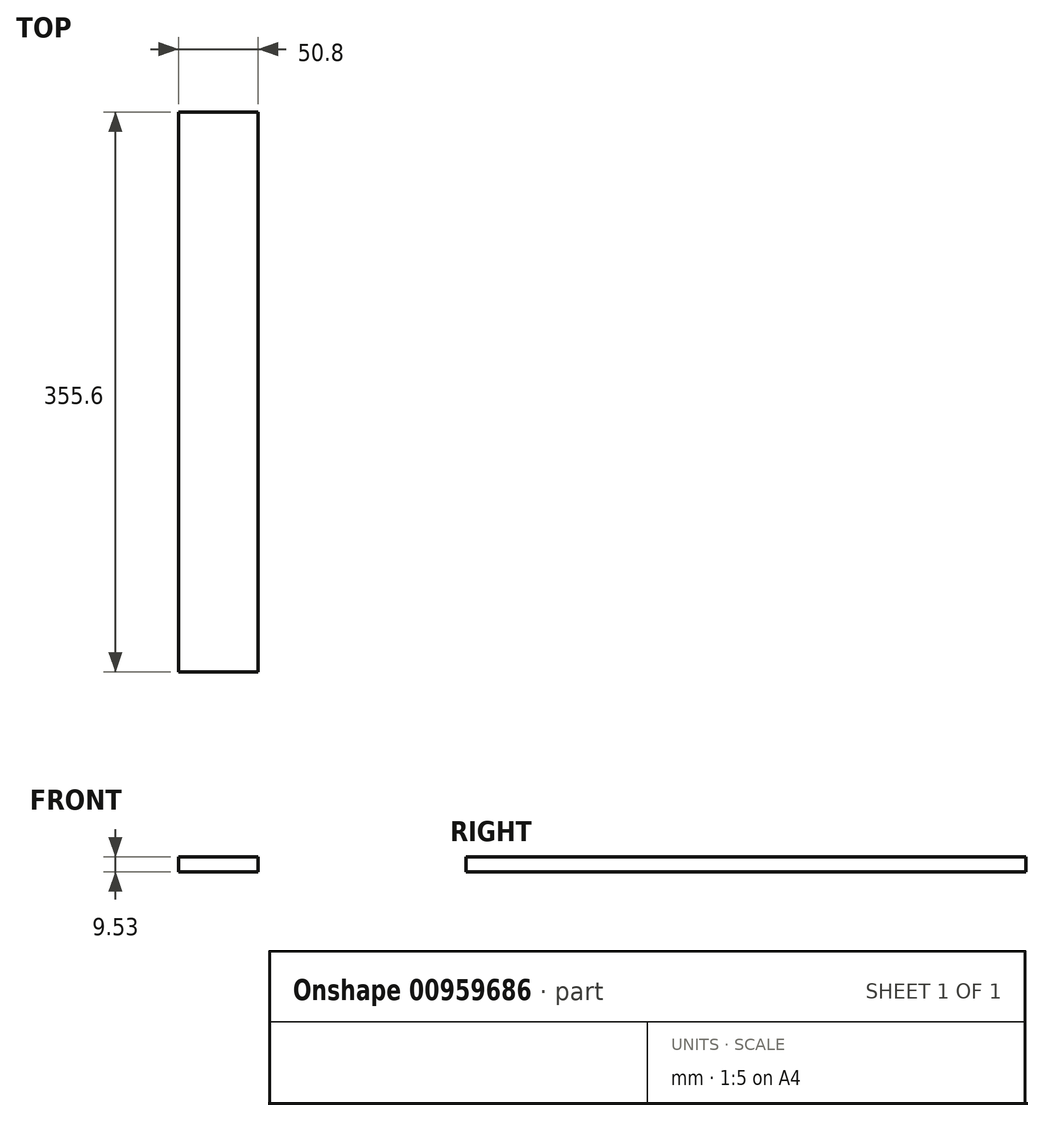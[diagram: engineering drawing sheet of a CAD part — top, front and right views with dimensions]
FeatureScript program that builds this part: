
annotation { "Feature Type Name" : "Feature", "Feature Type Description" : "" }
export const myFeature = defineFeature(function(context is Context, id is Id, definition is map)
    precondition{}
    {
        {
            var Q0;
            Q0=qCreatedBy(makeId("Top.planeOp"),FACE);
            var sketch = newSketch(context, id + "F0", { "sketchPlane" : qUnion([Q0])});
            skLineSegment(sketch, "E0.bottom", {"start": v(-1799.8, 176.9) * mm, "end": v(-1749, 176.9) * mm});
            skLineSegment(sketch, "E0.top", {"start": v(-1799.8, -178.7) * mm, "end": v(-1749, -178.7) * mm});
            skLineSegment(sketch, "E0.left", {"start": v(-1799.8, 176.9) * mm, "end": v(-1799.8, -178.7) * mm});
            skLineSegment(sketch, "E0.right", {"start": v(-1749, 176.9) * mm, "end": v(-1749, -178.7) * mm});
            skSolve(sketch);
        }
        {
            var Q0;
            Q0=makeQuery(id+"F0.imprint","IMPRINT",FACE,{"disambiguationData":[TD([[makeQuery(id+"F0.imprint","IMPRINT",EDGE,{"derivedFrom":sQuery(id+"F0.wireOp",EDGE,"E0.bottom")}),-1.0]])]});
            extrude(context, id + "F1", {"entities" : qUnion([Q0]), "depth" : 9.52 * mm, "offsetDistance" : 25.4 * mm});
        }
    });
